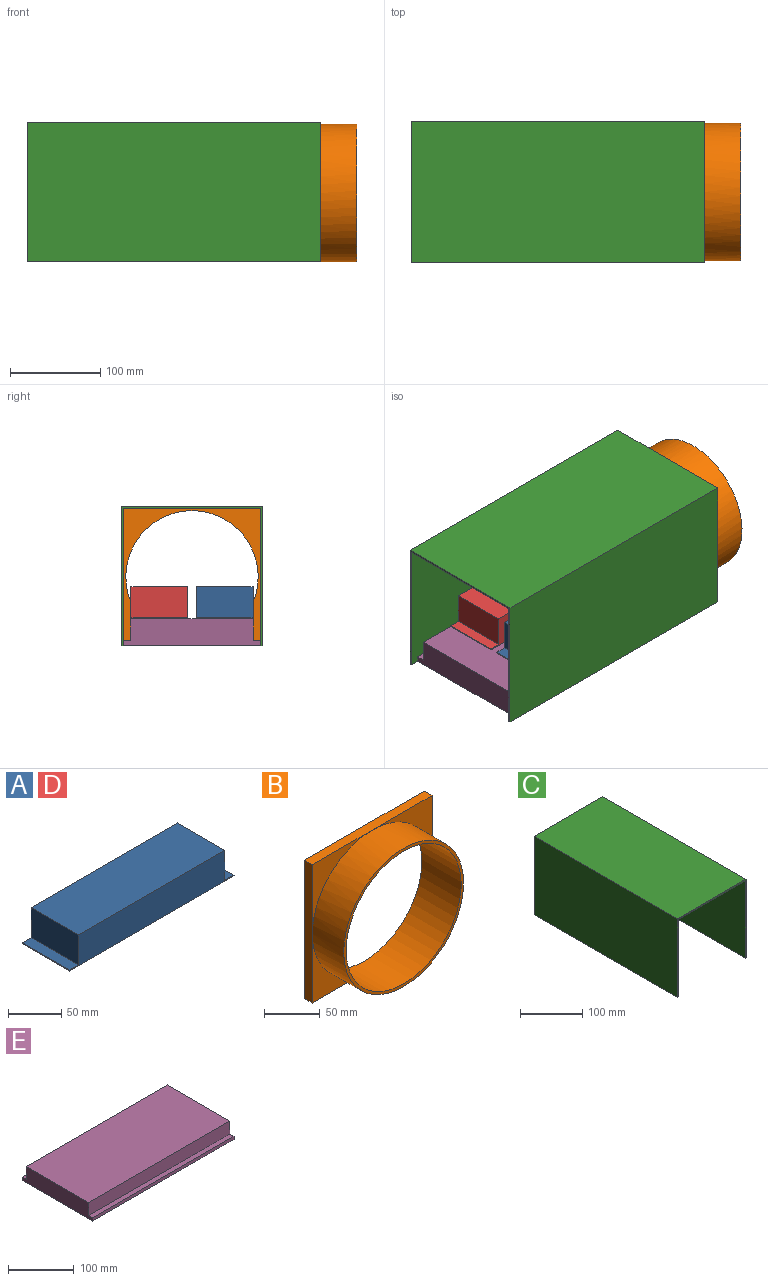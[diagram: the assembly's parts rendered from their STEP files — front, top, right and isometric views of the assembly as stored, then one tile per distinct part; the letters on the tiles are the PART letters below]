
ASSEMBLY  parts=5 mates=4
PART A: 10 faces, bbox 219x63x35.5 mm
  f0: plane 63x12mm, normal (0,0,1), area 756mm2, adj f1,f2,f3,f7
  f1: plane 219x35.5mm, normal (0,1,0), area 6946.5mm2, adj f0,f2,f4,f5,f6,f7,f8,f9
  f2: plane 63x1mm, normal (-1,0,0), area 63mm2, adj f0,f1,f3,f6
  f3: plane 219x35.5mm, normal (0,-1,0), area 6946.5mm2, adj f0,f2,f4,f5,f6,f7,f8,f9
  f4: plane 63x1mm, normal (1,0,0), area 63mm2, adj f1,f3,f5,f6
  f5: plane 63x12mm, normal (0,0,1), area 756mm2, adj f1,f3,f4,f8
  f6: plane 219x63mm, normal (0,0,-1), area 13797mm2, adj f1,f2,f3,f4
  f7: plane 63x34.5mm, normal (-1,0,0), area 2173.5mm2, adj f0,f1,f3,f9
  f8: plane 63x34.5mm, normal (1,0,0), area 2173.5mm2, adj f1,f3,f5,f9
  f9: plane 195x63mm, normal (0,0,1), area 12285mm2, adj f1,f3,f7,f8
PART B: 12 faces, bbox 152.4x50x152.4 mm
  f0: plane 76.2x76.2mm, normal (0,-1,0), area 1246.1mm2, adj f4,f5,f10
  f1: plane 76.2x76.2mm, normal (0,-1,0), area 1246.1mm2, adj f3,f4,f10
  f2: plane 76.2x76.2mm, normal (0,-1,0), area 1246.1mm2, adj f3,f6,f10
  f3: plane 152.4x10mm, normal (0,0,1), area 1524mm2, adj f1,f2,f4,f6,f9
  f4: plane 152.4x10mm, normal (-1,0,0), area 1524mm2, adj f0,f1,f3,f5,f9
  f5: plane 152.4x10mm, normal (0,0,-1), area 1524mm2, adj f0,f4,f6,f8,f9
  f6: plane 152.4x10mm, normal (1,0,0), area 1524mm2, adj f2,f3,f5,f8,f9
  f7: cylinder r=73.2mm len=146.4mm, axis (0,1,0), area 22996.5mm2, adj f9,f11
  f8: plane 76.2x76.2mm, normal (0,-1,0), area 1246.1mm2, adj f5,f6,f10
  f9: plane 152.4x152.4mm, normal (0,1,0), area 6392.4mm2, adj f3,f4,f5,f6,f7
  f10: cylinder r=76.2mm len=152.4mm, axis (0,1,0), area 19151.1mm2, adj f0,f1,f2,f8,f11
  f11: plane 152.4x152.4mm, normal (0,-1,0), area 1408.1mm2, adj f7,f10
PART C: 10 faces, bbox 156.4x325x154.4 mm
  f0: plane 325x152.4mm, normal (1,0,0), area 49530mm2, adj f1,f7,f8,f9
  f1: plane 325x152.4mm, normal (0,0,-1), area 49530mm2, adj f0,f2,f8,f9
  f2: plane 325x152.4mm, normal (-1,0,0), area 49530mm2, adj f1,f3,f8,f9
  f3: plane 325x2mm, normal (0,0,-1), area 650mm2, adj f2,f4,f8,f9
  f4: plane 325x154.4mm, normal (1,0,0), area 50180mm2, adj f3,f5,f8,f9
  f5: plane 325x156.4mm, normal (0,0,1), area 50830mm2, adj f4,f6,f8,f9
  f6: plane 325x154.4mm, normal (-1,0,0), area 50180mm2, adj f5,f7,f8,f9
  f7: plane 325x2mm, normal (0,0,-1), area 650mm2, adj f0,f6,f8,f9
  f8: plane 156.4x154.4mm, normal (0,-1,0), area 922.4mm2, adj f0,f1,f2,f3,f4,f5,f6,f7
  f9: plane 156.4x154.4mm, normal (0,1,0), area 922.4mm2, adj f0,f1,f2,f3,f4,f5,f6,f7
PART D: same geometry as A
PART E: 10 faces, bbox 304.8x152.4x30 mm
  f0: plane 304.8x8.7mm, normal (0,0,1), area 2651.8mm2, adj f1,f7,f8,f9
  f1: plane 304.8x24.13mm, normal (0,1,0), area 7354.8mm2, adj f0,f2,f8,f9
  f2: plane 304.8x135mm, normal (0,0,1), area 41148mm2, adj f1,f3,f8,f9
  f3: plane 304.8x24.13mm, normal (0,-1,0), area 7354.8mm2, adj f2,f4,f8,f9
  f4: plane 304.8x8.7mm, normal (0,0,1), area 2651.8mm2, adj f3,f5,f8,f9
  f5: plane 304.8x5.84mm, normal (0,-1,0), area 1780.6mm2, adj f4,f6,f8,f9
  f6: plane 304.8x152.4mm, normal (0,0,-1), area 46451.5mm2, adj f5,f7,f8,f9
  f7: plane 304.8x5.84mm, normal (0,1,0), area 1780.6mm2, adj f0,f6,f8,f9
  f8: plane 152.4x29.97mm, normal (1,0,0), area 4147.9mm2, adj f0,f1,f2,f3,f4,f5,f6,f7
  f9: plane 152.4x29.97mm, normal (-1,0,0), area 4147.9mm2, adj f0,f1,f2,f3,f4,f5,f6,f7
PLACE A t=(132.62,-3.87,40)mm
PLACE B rot(axis=(0,0,1),90deg) t=(394.52,63.63,92.1)mm
PLACE C rot(axis=(0,0,1),90deg) t=(79.62,63.63,162.43)mm
PLACE D t=(132.62,68.13,40)mm
PLACE E t=(89.72,-12.57,10.03)mm
MATE planar C.f2 <-> E.f7  axis (0,-1,0) through (242.12,139.83,10.03)mm
MATE planar E.f8 <-> B.f9  axis (1,0,0) through (394.52,63.63,10.03)mm
MATE planar E.f2 <-> A.f6  axis (0,0,1) through (242.12,-3.87,40)mm
MATE planar D.f6 <-> E.f2  axis (0,0,-1) through (242.12,131.13,40)mm
